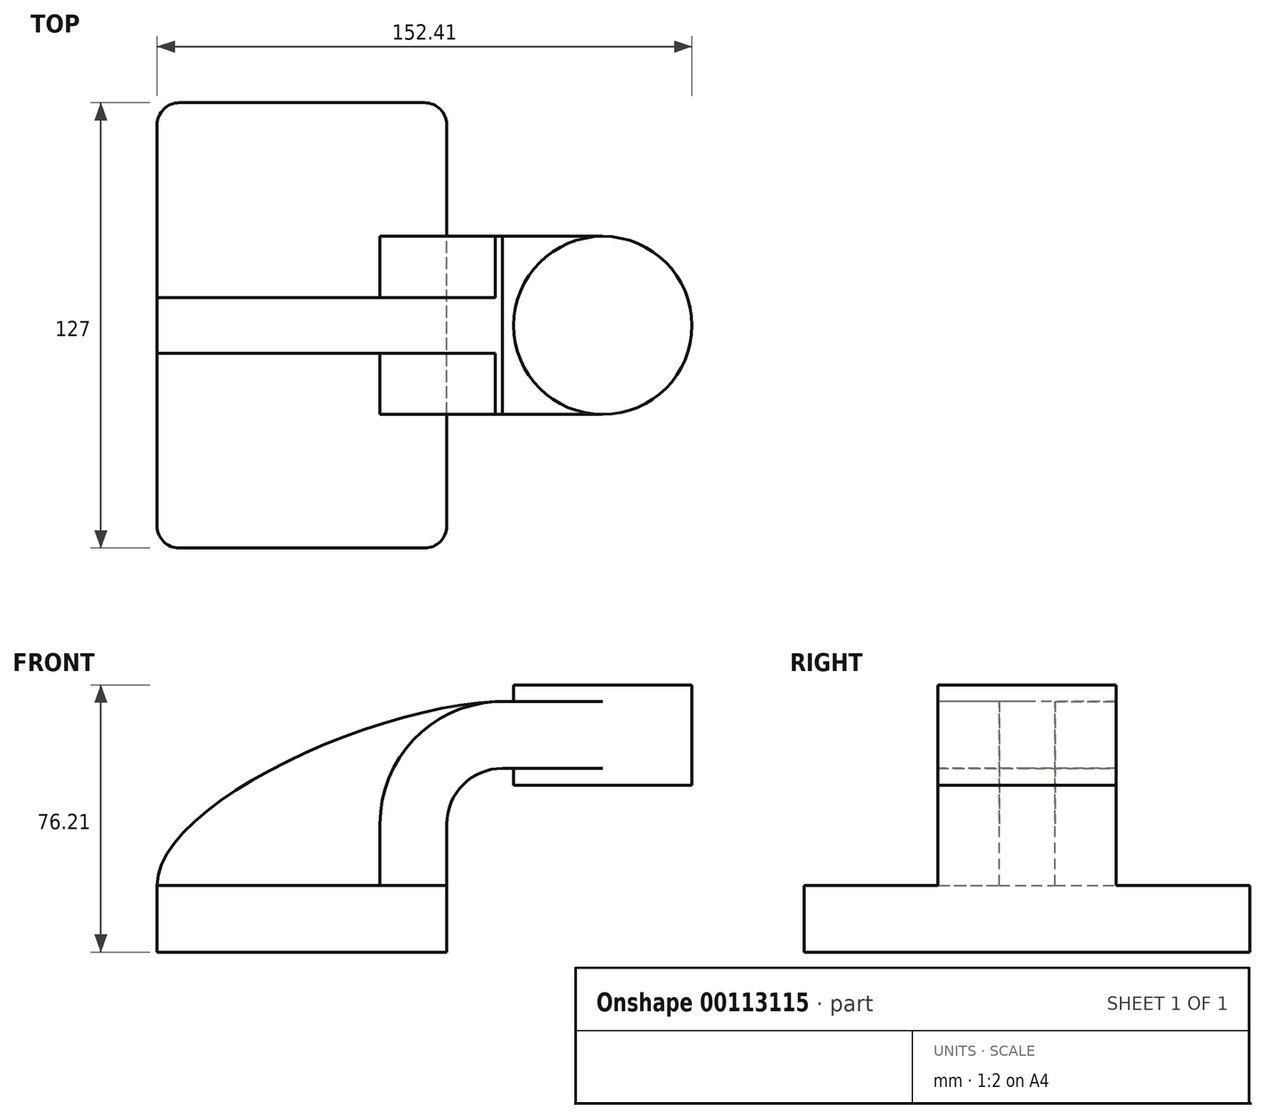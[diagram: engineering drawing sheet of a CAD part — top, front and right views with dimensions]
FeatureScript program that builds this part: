
annotation { "Feature Type Name" : "Feature", "Feature Type Description" : "" }
export const myFeature = defineFeature(function(context is Context, id is Id, definition is map)
    precondition{}
    {
        {
            var Q0;
            Q0=qCreatedBy(makeId("Front.planeOp"),FACE);
            var sketch = newSketch(context, id + "F0", { "sketchPlane" : qUnion([Q0])});
            skLineSegment(sketch, "E0.bottom", {"start": v(41.28, -9.52) * mm, "end": v(-41.28, -9.53) * mm});
            skLineSegment(sketch, "E0.top", {"start": v(41.28, 9.53) * mm, "end": v(-41.28, 9.53) * mm});
            skLineSegment(sketch, "E0.left", {"start": v(41.28, -9.52) * mm, "end": v(41.28, 9.53) * mm});
            skLineSegment(sketch, "E0.right", {"start": v(-41.28, -9.53) * mm, "end": v(-41.28, 9.53) * mm});
            skPoint(sketch, "E0.middle", {"position": v(0, 0) * mm});
            skLineSegment(sketch, "E1.bottom", {"start": v(111.12, 38.1) * mm, "end": v(60.33, 38.1) * mm});
            skLineSegment(sketch, "E1.top", {"start": v(111.12, 66.68) * mm, "end": v(60.33, 66.68) * mm});
            skLineSegment(sketch, "E1.left", {"start": v(111.12, 38.1) * mm, "end": v(111.12, 66.68) * mm});
            skLineSegment(sketch, "E1.right", {"start": v(60.33, 38.1) * mm, "end": v(60.33, 66.68) * mm});
            skPoint(sketch, "E1.middle", {"position": v(85.72, 52.39) * mm});
            skLineSegment(sketch, "E2", {"start": v(41.28, 9.53) * mm, "end": v(41.28, 27) * mm});
            skArc(sketch, "E3", {"start": v(41.27, 27) * mm, "mid": v(45.92, 38.23) * mm, "end": v(57.15, 42.88) * mm});
            skLineSegment(sketch, "E4", {"start": v(57.15, 42.88) * mm, "end": v(85.72, 42.88) * mm});
            skLineSegment(sketch, "E5.0", {"start": v(57.15, 61.93) * mm, "end": v(85.72, 61.93) * mm});
            skArc(sketch, "E5.1", {"start": v(22.22, 27) * mm, "mid": v(32.45, 51.7) * mm, "end": v(57.15, 61.93) * mm});
            skLineSegment(sketch, "E5.2", {"start": v(22.22, 9.53) * mm, "end": v(22.22, 27) * mm});
            skFitSpline(sketch, "E6", {"points": [v(-41.28, 9.53) * mm, v(57.15, 61.93) * mm], "startDerivative": vector(-0.99, 68.3) * mm, "endDerivative": vector(108.6, 1.61) * mm});
            skLineSegment(sketch, "E7", {"start": v(85.72, 38.1) * mm, "end": v(85.72, 66.68) * mm});
            skSolve(sketch);
        }
        {
            var Q0;
            Q0=makeQuery(id+"F0.imprint","IMPRINT",FACE,{"disambiguationData":[TD([[makeQuery(id+"F0.imprint","IMPRINT",EDGE,{"derivedFrom":sQuery(id+"F0.wireOp",EDGE,"E0.bottom")}),-1.0]])]});
            extrude(context, id + "F1", {"entities" : qUnion([Q0]), "endBound" : BoundingType.SYMMETRIC, "depth" : 127 * mm});
        }
        {
            var Q0;
            {var subQ1=sQuery(id+"F0.wireOp",EDGE,"E2");Q0=makeQuery(id+"F0.imprint","IMPRINT",FACE,{"disambiguationData":[TD([[makeQuery(id+"F0.imprint","IMPRINT",EDGE,{"derivedFrom":subQ1}),1.0]])]});}
            var Q1;
            {var subQ5=sQuery(id+"F0.wireOp",EDGE,"E1.right");var subQ7=sQuery(id+"F0.wireOp",EDGE,"E4");var subQ9=makeQuery(id+"F0.imprint","INTERSECT",VERTEX,{"derivedFrom":[subQ5,subQ7]});Q1=makeQuery(id+"F0.imprint","IMPRINT",FACE,{"disambiguationData":[TD([[makeQuery(id+"F0.imprint","IMPRINT",EDGE,{"disambiguationData":[TD([[subQ9,-1.0]])],"derivedFrom":subQ5}),-1.0]])]});}
            extrude(context, id + "F2", {"entities" : qUnion([Q0, Q1]), "operationType" : NewBodyOperationType.ADD, "endBound" : BoundingType.SYMMETRIC, "depth" : 50.8 * mm});
        }
        {
            var Q0;
            {var subQ3=sQuery(id+"F0.wireOp",EDGE,"E5.2");Q0=makeQuery(id+"F0.imprint","IMPRINT",FACE,{"disambiguationData":[TD([[makeQuery(id+"F0.imprint","IMPRINT",EDGE,{"derivedFrom":subQ3}),1.0]])]});}
            extrude(context, id + "F3", {"entities" : qUnion([Q0]), "operationType" : NewBodyOperationType.ADD, "endBound" : BoundingType.SYMMETRIC, "depth" : 15.88 * mm});
        }
        {
            var Q0;
            Q0=makeQuery(id+"F1.opExtrude","CAP_EDGE",EDGE,{"disambiguationData":[OSD([sQuery(id+"F0.wireOp",EDGE,"E0.right")])],"isStart":false});
            var Q1;
            Q1=makeQuery(id+"F1.opExtrude","CAP_EDGE",EDGE,{"disambiguationData":[OSD([sQuery(id+"F0.wireOp",EDGE,"E0.left")])],"isStart":false});
            var Q2;
            Q2=makeQuery(id+"F1.opExtrude","CAP_EDGE",EDGE,{"disambiguationData":[OSD([sQuery(id+"F0.wireOp",EDGE,"E0.left")])],"isStart":true});
            var Q3;
            Q3=makeQuery(id+"F1.opExtrude","CAP_EDGE",EDGE,{"disambiguationData":[OSD([sQuery(id+"F0.wireOp",EDGE,"E0.right")])],"isStart":true});
            fillet(context, id + "F4", {"entities" : qUnion([Q0, Q1, Q2, Q3]), "radius" : 6.35 * mm, "tangentPropagation" : true, "allowEdgeOverflow" : false});
        }
        {
            var Q0;
            {var subQ4=sQuery(id+"F0.wireOp",EDGE,"E1.left");Q0=makeQuery(id+"F0.imprint","IMPRINT",FACE,{"disambiguationData":[TD([[makeQuery(id+"F0.imprint","IMPRINT",EDGE,{"derivedFrom":subQ4}),1.0]])]});}
            var Q1;
            Q1=sQuery(id+"F0.wireOp",EDGE,"E7");
            revolve(context, id + "F5", {"operationType" : NewBodyOperationType.ADD, "entities" : qUnion([Q0]), "axis" : qUnion([Q1]), "revolveType" : RevolveType.FULL});
        }
    });
